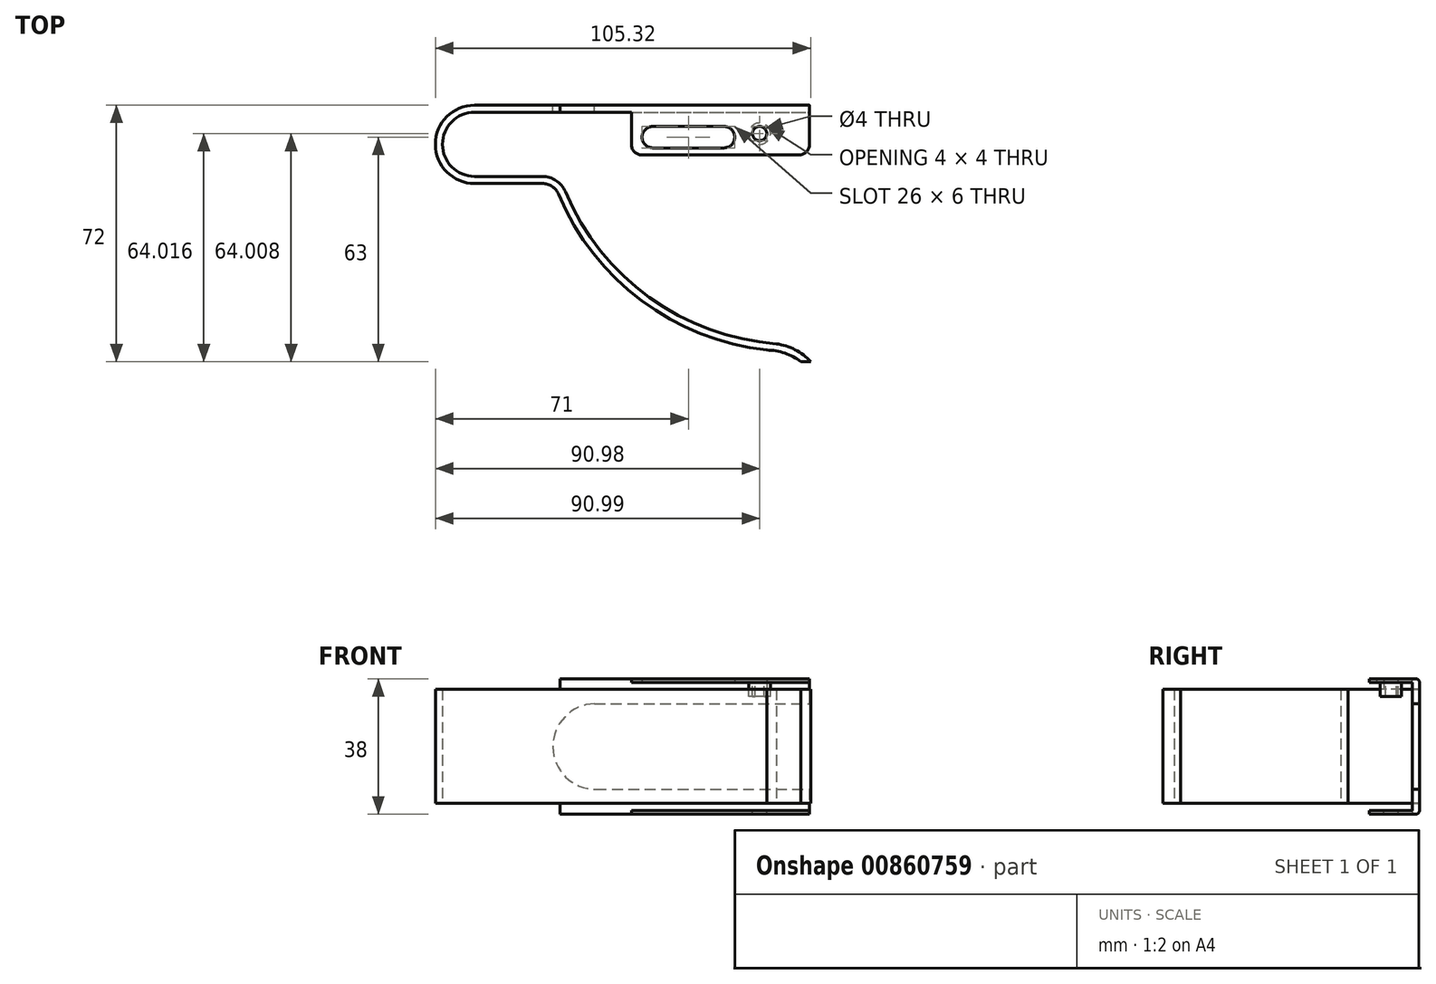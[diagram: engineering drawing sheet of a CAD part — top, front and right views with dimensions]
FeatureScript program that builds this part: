
annotation { "Feature Type Name" : "Feature", "Feature Type Description" : "" }
export const myFeature = defineFeature(function(context is Context, id is Id, definition is map)
    precondition{}
    {
        {
            var Q0;
            Q0=qCreatedBy(makeId("Top.planeOp"),FACE);
            var sketch = newSketch(context, id + "F0", { "sketchPlane" : qUnion([Q0])});
            skArc(sketch, "E0", {"start": v(0, 11) * mm, "mid": v(-11, 0) * mm, "end": v(0, -11) * mm});
            skLineSegment(sketch, "E1", {"start": v(0, 11) * mm, "end": v(94, 11) * mm});
            skLineSegment(sketch, "E2", {"start": v(0, -11) * mm, "end": v(19, -11) * mm});
            skArc(sketch, "E3", {"start": v(23.61, -14.06) * mm, "mid": v(46.86, -43.85) * mm, "end": v(82, -57.75) * mm});
            skPoint(sketch, "E4.visualSharp", {"position": v(22.4, -11) * mm});
            skArc(sketch, "E4.filletArc", {"start": v(23.61, -14.06) * mm, "mid": v(21.77, -11.84) * mm, "end": v(19, -11) * mm});
            skLineSegment(sketch, "E5.0", {"start": v(0, 9) * mm, "end": v(94, 9) * mm});
            skArc(sketch, "E5.1", {"start": v(25.45, -13.3) * mm, "mid": v(49.07, -42.99) * mm, "end": v(84.7, -56) * mm});
            skArc(sketch, "E5.2", {"start": v(25.45, -13.3) * mm, "mid": v(22.88, -10.17) * mm, "end": v(19, -9) * mm});
            skLineSegment(sketch, "E5.3", {"start": v(0, -9) * mm, "end": v(19, -9) * mm});
            skArc(sketch, "E5.4", {"start": v(0, 9) * mm, "mid": v(-9, 0) * mm, "end": v(0, -9) * mm});
            skLineSegment(sketch, "E6", {"start": v(94, 11) * mm, "end": v(94, 9) * mm});
            skArc(sketch, "E7", {"start": v(91.6, -61) * mm, "mid": v(87.06, -58.6) * mm, "end": v(82, -57.75) * mm});
            skArc(sketch, "E8.0", {"start": v(94.32, -61) * mm, "mid": v(89.95, -57.66) * mm, "end": v(84.7, -56) * mm});
            skLineSegment(sketch, "E9", {"start": v(91.6, -61) * mm, "end": v(94.32, -61) * mm});
            skSolve(sketch);
        }
        {
            var Q0;
            Q0=qSketchRegion(id+"F0",true);
            extrude(context, id + "F1", {"entities" : qUnion([Q0]), "depth" : 16 * mm, "offsetDistance" : 25 * mm});
        }
        {
            var Q0;
            Q0=makeQuery(id+"F1.opExtrude","SWEPT_FACE",FACE,{"disambiguationData":[OSD([sQuery(id+"F0.wireOp",EDGE,"E1")])]});
            var sketch = newSketch(context, id + "F2", { "sketchPlane" : qUnion([Q0])});
            skLineSegment(sketch, "E10.bottom", {"start": v(-94, 16) * mm, "end": v(-24, 16) * mm});
            skLineSegment(sketch, "E10.top", {"start": v(-94, 19) * mm, "end": v(-24, 19) * mm});
            skLineSegment(sketch, "E10.left", {"start": v(-94, 16) * mm, "end": v(-94, 19) * mm});
            skLineSegment(sketch, "E10.right", {"start": v(-24, 16) * mm, "end": v(-24, 19) * mm});
            skSolve(sketch);
        }
        {
            var Q0;
            Q0=qSketchRegion(id+"F2",true);
            var Q1;
            Q1 = qSketchRegion(id + "F4", true);
            extrude(context, id + "F3", {"entities" : qUnion([Q0, Q1]), "operationType" : NewBodyOperationType.ADD, "oppositeDirection" : true, "depth" : 2 * mm, "offsetDistance" : 25 * mm});
        }
        {
            var Q0;
            Q0=makeQuery(id+"F3.opExtrude","SWEPT_FACE",FACE,{"disambiguationData":[OSD([sQuery(id+"F2.wireOp",EDGE,"E10.top")])]});
            var sketch = newSketch(context, id + "F4", { "sketchPlane" : qUnion([Q0])});
            skLineSegment(sketch, "E11.bottom", {"start": v(44, 11) * mm, "end": v(94, 11) * mm});
            skLineSegment(sketch, "E11.top", {"start": v(44, -3) * mm, "end": v(94, -3) * mm});
            skLineSegment(sketch, "E11.left", {"start": v(44, 11) * mm, "end": v(44, -3) * mm});
            skLineSegment(sketch, "E11.right", {"start": v(94, 11) * mm, "end": v(94, -3) * mm});
            skSolve(sketch);
        }
        {
            var Q0;
            Q0=qSketchRegion(id+"F4",true);
            extrude(context, id + "F5", {"entities" : qUnion([Q0]), "operationType" : NewBodyOperationType.ADD, "oppositeDirection" : true, "depth" : 1 * mm, "offsetDistance" : 25 * mm});
        }
        {
            var Q0;
            Q0=makeQuery(id+"F5.opExtrude","CAP_EDGE",EDGE,{"disambiguationData":[OSD([sQuery(id+"F4.wireOp",EDGE,"E11.bottom")])],"isStart":false});
            var Q1;
            Q1=makeQuery(id+"F3.opExtrude","CAP_EDGE",EDGE,{"disambiguationData":[OSD([sQuery(id+"F2.wireOp",EDGE,"E10.top")])],"isStart":true});
            fillet(context, id + "F6", {"entities" : qUnion([Q0, Q1]), "radius" : 1 * mm, "tangentPropagation" : true, "allowEdgeOverflow" : false});
        }
        {
            var Q0;
            Q0=makeQuery(id+"F1.opExtrude","SWEPT_BODY",BODY,{"disambiguationData":[OSD([sQuery(id+"F0.wireOp",EDGE,"E0"),sQuery(id+"F0.wireOp",EDGE,"E1"),sQuery(id+"F0.wireOp",EDGE,"E2"),sQuery(id+"F0.wireOp",EDGE,"E3"),sQuery(id+"F0.wireOp",EDGE,"E4.filletArc"),sQuery(id+"F0.wireOp",EDGE,"E5.0"),sQuery(id+"F0.wireOp",EDGE,"E5.1"),sQuery(id+"F0.wireOp",EDGE,"E5.2"),sQuery(id+"F0.wireOp",EDGE,"E5.3"),sQuery(id+"F0.wireOp",EDGE,"E5.4"),sQuery(id+"F0.wireOp",EDGE,"E6"),sQuery(id+"F0.wireOp",EDGE,"E7"),sQuery(id+"F0.wireOp",EDGE,"E8.0"),sQuery(id+"F0.wireOp",EDGE,"E9")])]});
            var Q1;
            Q1=makeQuery(id+"F1.opExtrude","CAP_FACE",FACE,{"disambiguationData":[OSD([sQuery(id+"F0.wireOp",EDGE,"E0"),sQuery(id+"F0.wireOp",EDGE,"E1"),sQuery(id+"F0.wireOp",EDGE,"E2"),sQuery(id+"F0.wireOp",EDGE,"E3"),sQuery(id+"F0.wireOp",EDGE,"E4.filletArc"),sQuery(id+"F0.wireOp",EDGE,"E5.0"),sQuery(id+"F0.wireOp",EDGE,"E5.1"),sQuery(id+"F0.wireOp",EDGE,"E5.2"),sQuery(id+"F0.wireOp",EDGE,"E5.3"),sQuery(id+"F0.wireOp",EDGE,"E5.4"),sQuery(id+"F0.wireOp",EDGE,"E6"),sQuery(id+"F0.wireOp",EDGE,"E7"),sQuery(id+"F0.wireOp",EDGE,"E8.0"),sQuery(id+"F0.wireOp",EDGE,"E9")])],"isStart":true});
            mirror(context, id + "F7", {"operationType" : NewBodyOperationType.ADD, "entities" : qUnion([Q0]), "mirrorPlane" : qUnion([Q1])});
        }
        {
            var Q0;
            {var subQ0=makeQuery(id+"F3.boolean.opBoolean","MERGE",FACE,{"derivedFrom":[makeQuery(id+"F1.opExtrude","SWEPT_FACE",FACE,{"disambiguationData":[OSD([sQuery(id+"F0.wireOp",EDGE,"E1")])]}),makeQuery(id+"F3.opExtrude","CAP_FACE",FACE,{"disambiguationData":[OSD([sQuery(id+"F2.wireOp",EDGE,"E10.bottom"),sQuery(id+"F2.wireOp",EDGE,"E10.top"),sQuery(id+"F2.wireOp",EDGE,"E10.left"),sQuery(id+"F2.wireOp",EDGE,"E10.right")])],"isStart":true})]});Q0=makeQuery(id+"F7.boolean.opBoolean","MERGE",FACE,{"derivedFrom":[subQ0,makeQuery(id+"F7.opPattern","COPY",FACE,{"derivedFrom":subQ0,"instanceName":"1"})]});}
            var sketch = newSketch(context, id + "F8", { "sketchPlane" : qUnion([Q0])});
            skArc(sketch, "E12", {"start": v(-34, -12) * mm, "mid": v(-22, 0.16) * mm, "end": v(-34.33, 12) * mm});
            skLineSegment(sketch, "E13", {"start": v(-33.67, 12) * mm, "end": v(-94, 12) * mm});
            skLineSegment(sketch, "E14", {"start": v(-34, -12) * mm, "end": v(-94, -12) * mm});
            skSolve(sketch);
        }
        {
            var Q0;
            {var subQ0=sQuery(id+"F8.wireOp",EDGE,"E14");Q0=makeQuery(id+"F8.imprint","IMPRINT",FACE,{"disambiguationData":[TD([[makeQuery(id+"F8.imprint","IMPRINT",EDGE,{"derivedFrom":subQ0}),-1.0]])]});}
            extrude(context, id + "F9", {"entities" : qUnion([Q0]), "operationType" : NewBodyOperationType.REMOVE, "oppositeDirection" : true, "depth" : 2 * mm, "offsetDistance" : 25 * mm});
        }
        {
            var Q0;
            Q0=makeQuery(id+"F5.opExtrude","CAP_FACE",FACE,{"disambiguationData":[OSD([sQuery(id+"F4.wireOp",EDGE,"E11.bottom"),sQuery(id+"F4.wireOp",EDGE,"E11.top"),sQuery(id+"F4.wireOp",EDGE,"E11.left"),sQuery(id+"F4.wireOp",EDGE,"E11.right")])],"isStart":false});
            var sketch = newSketch(context, id + "F10", { "sketchPlane" : qUnion([Q0])});
            skLineSegment(sketch, "E15", {"start": v(50, -2) * mm, "end": v(70, -2) * mm});
            skArc(sketch, "E16.0.startCap", {"start": v(50, -5) * mm, "mid": v(47, -2) * mm, "end": v(50, 1) * mm});
            skArc(sketch, "E16.0.endCap", {"start": v(70, 1) * mm, "mid": v(73, -2) * mm, "end": v(70, -5) * mm});
            skLineSegment(sketch, "E16.0.left", {"start": v(50, 1) * mm, "end": v(70, 1) * mm});
            skLineSegment(sketch, "E16.0.right", {"start": v(50, -5) * mm, "end": v(70, -5) * mm});
            skSolve(sketch);
        }
        {
            var Q0;
            Q0=qSketchRegion(id+"F10",true);
            extrude(context, id + "F11", {"entities" : qUnion([Q0]), "operationType" : NewBodyOperationType.REMOVE, "endBound" : BoundingType.THROUGH_ALL, "oppositeDirection" : true, "depth" : 54.8 * mm, "offsetDistance" : 25 * mm});
        }
        {
            var Q0;
            Q0=makeQuery(id+"F5.opExtrude","CAP_FACE",FACE,{"disambiguationData":[OSD([sQuery(id+"F4.wireOp",EDGE,"E11.bottom"),sQuery(id+"F4.wireOp",EDGE,"E11.top"),sQuery(id+"F4.wireOp",EDGE,"E11.left"),sQuery(id+"F4.wireOp",EDGE,"E11.right")])],"isStart":false});
            var sketch = newSketch(context, id + "F12", { "sketchPlane" : qUnion([Q0])});
            skPoint(sketch, "E17", {"position": v(80, -3) * mm});
            skSolve(sketch);
        }
        {
            var Q0;
            Q0=sQuery(id+"F12.wireOp",VERTEX,"E17");
            var Q1;
            Q1=makeQuery(id+"F1.opExtrude","SWEPT_BODY",BODY,{"disambiguationData":[OSD([sQuery(id+"F0.wireOp",EDGE,"E0"),sQuery(id+"F0.wireOp",EDGE,"E1"),sQuery(id+"F0.wireOp",EDGE,"E2"),sQuery(id+"F0.wireOp",EDGE,"E3"),sQuery(id+"F0.wireOp",EDGE,"E4.filletArc"),sQuery(id+"F0.wireOp",EDGE,"E5.0"),sQuery(id+"F0.wireOp",EDGE,"E5.1"),sQuery(id+"F0.wireOp",EDGE,"E5.2"),sQuery(id+"F0.wireOp",EDGE,"E5.3"),sQuery(id+"F0.wireOp",EDGE,"E5.4"),sQuery(id+"F0.wireOp",EDGE,"E6"),sQuery(id+"F0.wireOp",EDGE,"E7"),sQuery(id+"F0.wireOp",EDGE,"E8.0"),sQuery(id+"F0.wireOp",EDGE,"E9")])]});
            hole(context, id + "F13", {"style" : HoleStyle.SIMPLE, "endStyle" : HoleEndStyle.BLIND, "holeDiameter" : 4 * mm, "majorDiameter" : 5 * mm, "holeDepth" : 50 * mm, "isTappedThrough" : true, "tappedDepth" : 12 * mm, "tapClearance" : 3, "locations" : qUnion([Q0]), "scope" : qUnion([Q1])});
        }
        {
            var Q0;
            Q0=makeQuery(id+"F5.opExtrude","CAP_FACE",FACE,{"disambiguationData":[OSD([sQuery(id+"F4.wireOp",EDGE,"E11.bottom"),sQuery(id+"F4.wireOp",EDGE,"E11.top"),sQuery(id+"F4.wireOp",EDGE,"E11.left"),sQuery(id+"F4.wireOp",EDGE,"E11.right")])],"isStart":true});
            var sketch = newSketch(context, id + "F14", { "sketchPlane" : qUnion([Q0])});
            skCircle(sketch, "E18.0", {"center": v(80, 3) * mm, "radius": 2 * mm});
            skCircle(sketch, "E19.0", {"center": v(80, 3) * mm, "radius": 3 * mm});
            skSolve(sketch);
        }
        {
            var Q0;
            Q0=qSketchRegion(id+"F14",true);
            extrude(context, id + "F15", {"entities" : qUnion([Q0]), "operationType" : NewBodyOperationType.ADD, "oppositeDirection" : true, "depth" : 5 * mm, "offsetDistance" : 25 * mm});
        }
        {
            var Q0;
            Q0=makeQuery(id+"F5.opExtrude","SWEPT_EDGE",EDGE,{"disambiguationData":[OSD([sQuery(id+"F4.wireOp",EDGE,"E11.top"),sQuery(id+"F4.wireOp",EDGE,"E11.right")])]});
            var Q1;
            Q1=makeQuery(id+"F5.opExtrude","SWEPT_EDGE",EDGE,{"disambiguationData":[OSD([sQuery(id+"F4.wireOp",EDGE,"E11.top"),sQuery(id+"F4.wireOp",EDGE,"E11.left")])]});
            var Q2;
            Q2=makeQuery(id+"F7.opPattern","COPY",EDGE,{"derivedFrom":makeQuery(id+"F5.opExtrude","SWEPT_EDGE",EDGE,{"disambiguationData":[OSD([sQuery(id+"F4.wireOp",EDGE,"E11.top"),sQuery(id+"F4.wireOp",EDGE,"E11.left")])]}),"instanceName":"1"});
            var Q3;
            Q3=makeQuery(id+"F7.opPattern","COPY",EDGE,{"derivedFrom":makeQuery(id+"F5.opExtrude","SWEPT_EDGE",EDGE,{"disambiguationData":[OSD([sQuery(id+"F4.wireOp",EDGE,"E11.top"),sQuery(id+"F4.wireOp",EDGE,"E11.right")])]}),"instanceName":"1"});
            fillet(context, id + "F16", {"entities" : qUnion([Q0, Q1, Q2, Q3]), "radius" : 3 * mm, "tangentPropagation" : true, "allowEdgeOverflow" : false});
        }
        {
            var Q0;
            Q0=makeQuery(id+"F5.boolean.opBoolean","MERGE",FACE,{"derivedFrom":[makeQuery(id+"F3.opExtrude","SWEPT_FACE",FACE,{"disambiguationData":[OSD([sQuery(id+"F2.wireOp",EDGE,"E10.top")])]}),makeQuery(id+"F5.opExtrude","CAP_FACE",FACE,{"disambiguationData":[OSD([sQuery(id+"F4.wireOp",EDGE,"E11.bottom"),sQuery(id+"F4.wireOp",EDGE,"E11.top"),sQuery(id+"F4.wireOp",EDGE,"E11.left"),sQuery(id+"F4.wireOp",EDGE,"E11.right")])],"isStart":true})]});
            var sketch = newSketch(context, id + "F17", { "sketchPlane" : qUnion([Q0])});
            skPoint(sketch, "E20", {"position": v(79.98, 3.02) * mm});
            skSolve(sketch);
        }
        {
            var Q0;
            Q0=sQuery(id+"F17.wireOp",VERTEX,"E20");
            var Q1;
            Q1=makeQuery(id+"F1.opExtrude","SWEPT_BODY",BODY,{"disambiguationData":[OSD([sQuery(id+"F0.wireOp",EDGE,"E0"),sQuery(id+"F0.wireOp",EDGE,"E1"),sQuery(id+"F0.wireOp",EDGE,"E2"),sQuery(id+"F0.wireOp",EDGE,"E3"),sQuery(id+"F0.wireOp",EDGE,"E4.filletArc"),sQuery(id+"F0.wireOp",EDGE,"E5.0"),sQuery(id+"F0.wireOp",EDGE,"E5.1"),sQuery(id+"F0.wireOp",EDGE,"E5.2"),sQuery(id+"F0.wireOp",EDGE,"E5.3"),sQuery(id+"F0.wireOp",EDGE,"E5.4"),sQuery(id+"F0.wireOp",EDGE,"E6"),sQuery(id+"F0.wireOp",EDGE,"E7"),sQuery(id+"F0.wireOp",EDGE,"E8.0"),sQuery(id+"F0.wireOp",EDGE,"E9")])]});
            hole(context, id + "F18", {"style" : HoleStyle.SIMPLE, "endStyle" : HoleEndStyle.BLIND, "holeDiameter" : 4 * mm, "majorDiameter" : 5 * mm, "holeDepth" : 50 * mm, "isTappedThrough" : true, "tappedDepth" : 12 * mm, "tapClearance" : 3, "locations" : qUnion([Q0]), "scope" : qUnion([Q1])});
        }
    });
